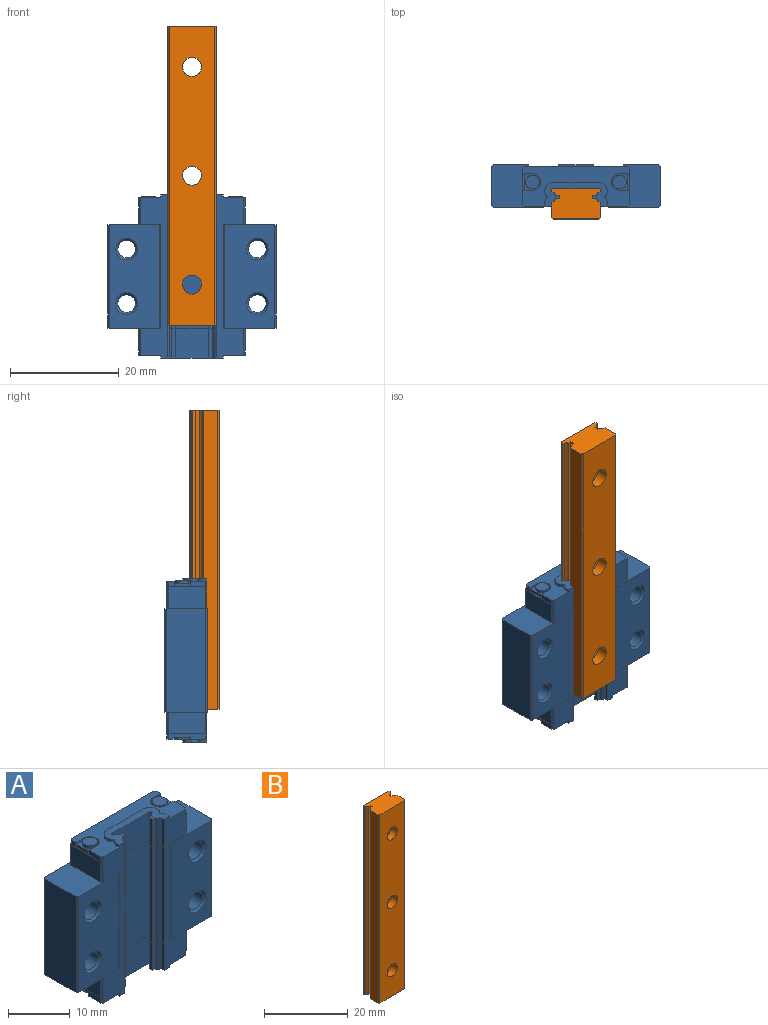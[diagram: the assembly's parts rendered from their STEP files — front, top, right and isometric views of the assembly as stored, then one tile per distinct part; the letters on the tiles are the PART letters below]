
ASSEMBLY  parts=2 mates=1
PART A: 236 faces, bbox 31x7.8x30 mm
  f0: plane 3.05x3mm, normal (0,0,-1), area 3.3mm2, adj f2,f74,f75,f95,f232
  f1: plane 3x0.6mm, normal (1,0,0), area 1.8mm2, adj f62,f68,f69,f235
  f2: plane 3x0.6mm, normal (-1,0,0), area 1.8mm2, adj f0,f62,f74,f75
  f3: plane 5.45x0.66mm, normal (1,0,0), area 3.6mm2, adj f112,f134,f145,f218
  f4: plane 5.45x0.66mm, normal (-1,0,0), area 3.6mm2, adj f19,f112,f144,f218
  f5: plane 19x0.66mm, normal (1,0,0), area 12.5mm2, adj f124,f134,f194,f217
  f6: plane 5.45x0.66mm, normal (1,0,0), area 3.6mm2, adj f113,f134,f157,f195
  f7: plane 5.45x0.66mm, normal (-1,0,0), area 3.6mm2, adj f19,f113,f163,f195
  f8: plane 2.5x2.5mm, normal (0,0,-1), area 4.9mm2, adj f228
  f9: plane 19x9.23mm, normal (0,-1,0), area 150.2mm2, adj f10,f17,f18,f31,f32,f227
  f10: cone r=1.62mm half-angle=45deg, axis (0,-1,0), area 6.1mm2, adj f9,f11
  f11: cylinder r=1.62mm len=7.04mm, axis (0,1,0), area 71.7mm2, adj f10,f12
  f12: cone r=2mm half-angle=45deg, axis (0,1,0), area 6.1mm2, adj f11,f13
  f13: plane 19x6.45mm, normal (0,1,0), area 97.4mm2, adj f12,f14,f15,f31,f32,f225
  f14: plane 19x0.25mm, normal (-0.71,0.71,0), area 6.7mm2, adj f13,f31,f32,f40
  f15: plane 19x0.3mm, normal (0.71,0.71,0), area 8.1mm2, adj f13,f16,f31,f32
  f16: plane 19x7.2mm, normal (1,0,0), area 136.8mm2, adj f15,f17,f31,f32
  f17: plane 19x0.3mm, normal (0.71,-0.71,0), area 8.1mm2, adj f9,f16,f31,f32
  f18: plane 19x0.21mm, normal (-0.42,-0.91,0), area 4.5mm2, adj f9,f19,f31,f32
  f19: plane 30x5mm, normal (0,-1,0), area 75mm2, adj f4,f7,f18,f27,f31,f32,f44,f48
  f20: plane 19x0.21mm, normal (0.42,-0.91,0), area 4.5mm2, adj f21,f31,f32,f134
  f21: plane 19x9.23mm, normal (0,-1,0), area 150.2mm2, adj f20,f22,f31,f32,f221,f224
  f22: plane 19x0.3mm, normal (-0.71,-0.71,0), area 8.1mm2, adj f21,f23,f31,f32
  f23: plane 19x7.2mm, normal (-1,0,0), area 136.8mm2, adj f22,f31,f32,f33
  f24: plane 19x4mm, normal (0,1,0), area 76mm2, adj f25,f30,f31,f96
  f25: plane 4x0.3mm, normal (0.71,0.71,0), area 1.7mm2, adj f24,f26,f31,f96
  f26: plane 6.8x4mm, normal (1,0,0), area 27.2mm2, adj f25,f27,f31,f96
  f27: plane 4x0.3mm, normal (0.71,-0.71,0), area 1.7mm2, adj f19,f26,f31,f96
  f28: plane 4x0.3mm, normal (-0.71,-0.71,0), area 1.7mm2, adj f29,f31,f96,f134
  f29: plane 6.8x4mm, normal (-1,0,0), area 27.2mm2, adj f28,f30,f31,f96
  f30: plane 4x0.3mm, normal (-0.71,0.71,0), area 1.7mm2, adj f24,f29,f31,f96
  f31: plane 31x7.8mm, normal (0,0,1), area 92.9mm2, adj f9,f13,f14,f15,f16,f17,f18,f19
  f32: plane 31x7.8mm, normal (0,0,-1), area 92.9mm2, adj f9,f13,f14,f15,f16,f17,f18,f19
  f33: plane 19x0.3mm, normal (-0.71,0.71,0), area 8.1mm2, adj f23,f31,f32,f34
  f34: plane 19x6.45mm, normal (0,1,0), area 97.4mm2, adj f31,f32,f33,f35,f219,f222
  f35: plane 19x0.25mm, normal (0.71,0.71,0), area 6.7mm2, adj f31,f32,f34,f36
  f36: plane 19x5.1mm, normal (0,1,0), area 96.9mm2, adj f31,f32,f35,f37
  f37: plane 19x0.25mm, normal (-0.71,0.71,0), area 6.7mm2, adj f31,f32,f36,f38
  f38: plane 19x6.3mm, normal (0,1,0), area 119.7mm2, adj f31,f32,f37,f39
  f39: plane 19x0.25mm, normal (0.71,0.71,0), area 6.7mm2, adj f31,f32,f38,f40
  f40: plane 19x5.1mm, normal (0,1,0), area 96.9mm2, adj f14,f31,f32,f39
  f41: plane 4x0.3mm, normal (-0.71,0.71,0), area 1.7mm2, adj f32,f42,f47,f62
  f42: plane 6.8x4mm, normal (-1,0,0), area 27.2mm2, adj f32,f41,f43,f62
  f43: plane 4x0.3mm, normal (-0.71,-0.71,0), area 1.7mm2, adj f32,f42,f62,f134
  f44: plane 4x0.3mm, normal (0.71,-0.71,0), area 1.7mm2, adj f19,f32,f45,f62
  f45: plane 6.8x4mm, normal (1,0,0), area 27.2mm2, adj f32,f44,f46,f62
  f46: plane 4x0.3mm, normal (0.71,0.71,0), area 1.7mm2, adj f32,f45,f47,f62
  f47: plane 19x4mm, normal (0,1,0), area 76mm2, adj f32,f41,f46,f62
  f48: plane 19.5x7.3mm, normal (0,0,1), area 75.5mm2, adj f19,f49,f50,f51,f52,f53,f54,f55
  f49: plane 0.5x0.15mm, normal (-1,0,0), area 0.1mm2, adj f48,f50,f61,f113
  f50: cylinder r=1.5mm len=1.5mm, axis (0,0,-1), area 1.2mm2, adj f48,f49,f51,f113
  f51: plane 8.46x0.5mm, normal (0,1,0), area 4.2mm2, adj f48,f50,f52,f113
  f52: cylinder r=1.5mm len=1.5mm, axis (0,0,-1), area 1.2mm2, adj f48,f51,f53,f113
  f53: plane 0.5x0.15mm, normal (1,0,0), area 0.1mm2, adj f48,f52,f54,f113
  f54: cylinder r=1.3mm len=1.01mm, axis (0,0,-1), area 0.6mm2, adj f48,f53,f55,f113
  f55: cylinder r=0.1mm len=0.5mm, axis (0,0,-1), area 0.1mm2, adj f48,f54,f56,f113
  f56: cylinder r=1.3mm len=1.01mm, axis (0,0,-1), area 0.6mm2, adj f48,f55,f57,f113
  f57: plane 0.62x0.5mm, normal (1,0,0), area 0.3mm2, adj f19,f48,f56,f113
  f58: plane 0.62x0.5mm, normal (-1,0,0), area 0.3mm2, adj f48,f59,f113,f134
  f59: cylinder r=1.3mm len=1.01mm, axis (0,0,-1), area 0.6mm2, adj f48,f58,f60,f113
  f60: cylinder r=0.1mm len=0.5mm, axis (0,0,-1), area 0.1mm2, adj f48,f59,f61,f113
  f61: cylinder r=1.3mm len=1.01mm, axis (0,0,-1), area 0.6mm2, adj f48,f49,f60,f113
  f62: plane 19.6x7.4mm, normal (0,0,-1), area 3.9mm2, adj f1,f2,f19,f41,f42,f43,f44,f45
  f63: plane 1x1mm, normal (-1,0,0), area 1mm2, adj f62,f64,f75,f76
  f64: plane 1x0.3mm, normal (-0.71,0.71,0), area 0.4mm2, adj f62,f63,f65,f76
  f65: plane 18.9x1mm, normal (0,1,0), area 18.9mm2, adj f62,f64,f66,f76
  f66: plane 1x0.3mm, normal (0.71,0.71,0), area 0.4mm2, adj f62,f65,f67,f76
  f67: plane 1x1mm, normal (1,0,0), area 1mm2, adj f62,f66,f68,f76
  f68: plane 1.75x1mm, normal (0,-1,0), area 0.8mm2, adj f1,f62,f67,f76,f94,f235
  f69: plane 1.75x1mm, normal (0,1,0), area 0.8mm2, adj f1,f62,f70,f76,f94,f235
  f70: plane 2.7x1mm, normal (1,0,0), area 2.7mm2, adj f62,f69,f71,f76
  f71: plane 1x0.3mm, normal (0.71,-0.71,0), area 0.4mm2, adj f19,f62,f70,f76
  f72: plane 1x0.3mm, normal (-0.71,-0.71,0), area 0.4mm2, adj f62,f73,f76,f134
  f73: plane 2.7x1mm, normal (-1,0,0), area 2.7mm2, adj f62,f72,f74,f76
  f74: plane 1.75x1mm, normal (0,1,0), area 0.8mm2, adj f0,f2,f62,f73,f76,f95
  f75: plane 1.75x1mm, normal (0,-1,0), area 0.8mm2, adj f0,f2,f62,f63,f76,f95
  f76: plane 19.5x7.3mm, normal (0,0,-1), area 75.5mm2, adj f19,f63,f64,f65,f66,f67,f68,f69
  f77: plane 0.5x0.15mm, normal (-1,0,0), area 0.1mm2, adj f76,f78,f89,f112
  f78: cylinder r=1.5mm len=1.5mm, axis (0,0,1), area 1.2mm2, adj f76,f77,f79,f112
  f79: plane 8.46x0.5mm, normal (0,1,0), area 4.2mm2, adj f76,f78,f80,f112
  f80: cylinder r=1.5mm len=1.5mm, axis (0,0,1), area 1.2mm2, adj f76,f79,f81,f112
  f81: plane 0.5x0.15mm, normal (1,0,0), area 0.1mm2, adj f76,f80,f82,f112
  f82: cylinder r=1.3mm len=1.01mm, axis (0,0,1), area 0.6mm2, adj f76,f81,f83,f112
  f83: cylinder r=0.1mm len=0.5mm, axis (0,0,1), area 0.1mm2, adj f76,f82,f84,f112
  f84: cylinder r=1.3mm len=1.01mm, axis (0,0,1), area 0.6mm2, adj f76,f83,f85,f112
  f85: plane 0.62x0.5mm, normal (1,0,0), area 0.3mm2, adj f19,f76,f84,f112
  f86: plane 0.62x0.5mm, normal (-1,0,0), area 0.3mm2, adj f76,f87,f112,f134
  f87: cylinder r=1.3mm len=1.01mm, axis (0,0,1), area 0.6mm2, adj f76,f86,f88,f112
  f88: cylinder r=0.1mm len=0.5mm, axis (0,0,1), area 0.1mm2, adj f76,f87,f89,f112
  f89: cylinder r=1.3mm len=1.01mm, axis (0,0,1), area 0.6mm2, adj f76,f77,f88,f112
  f90: plane 3x0.6mm, normal (-1,0,0), area 1.8mm2, adj f91,f96,f109,f111
  f91: plane 3.05x3mm, normal (0,0,1), area 3.3mm2, adj f90,f109,f110,f111,f233
  f92: plane 3x0.6mm, normal (1,0,0), area 1.8mm2, adj f93,f96,f102,f104
  f93: plane 3.05x3mm, normal (0,0,1), area 3.3mm2, adj f92,f102,f103,f104,f229
  f94: cylinder r=1.5mm len=3mm, axis (0,0,1), area 1.9mm2, adj f68,f69,f76,f235
  f95: cylinder r=1.5mm len=3mm, axis (0,0,1), area 1.9mm2, adj f0,f74,f75,f76
  f96: plane 19.6x7.4mm, normal (0,0,1), area 3.9mm2, adj f19,f24,f25,f26,f27,f28,f29,f30
  f97: plane 1x1mm, normal (-1,0,0), area 1mm2, adj f48,f96,f98,f111
  f98: plane 1x0.3mm, normal (-0.71,0.71,0), area 0.4mm2, adj f48,f96,f97,f99
  f99: plane 18.9x1mm, normal (0,1,0), area 18.9mm2, adj f48,f96,f98,f100
  f100: plane 1x0.3mm, normal (0.71,0.71,0), area 0.4mm2, adj f48,f96,f99,f101
  f101: plane 1x1mm, normal (1,0,0), area 1mm2, adj f48,f96,f100,f102
  f102: plane 1.75x1mm, normal (0,-1,0), area 0.8mm2, adj f48,f92,f93,f96,f101,f103
  f103: cylinder r=1.5mm len=3mm, axis (0,0,-1), area 1.9mm2, adj f48,f93,f102,f104
  f104: plane 1.75x1mm, normal (0,1,0), area 0.8mm2, adj f48,f92,f93,f96,f103,f105
  f105: plane 2.7x1mm, normal (1,0,0), area 2.7mm2, adj f48,f96,f104,f106
  f106: plane 1x0.3mm, normal (0.71,-0.71,0), area 0.4mm2, adj f19,f48,f96,f105
  f107: plane 1x0.3mm, normal (-0.71,-0.71,0), area 0.4mm2, adj f48,f96,f108,f134
  f108: plane 2.7x1mm, normal (-1,0,0), area 2.7mm2, adj f48,f96,f107,f109
  f109: plane 1.75x1mm, normal (0,1,0), area 0.8mm2, adj f48,f90,f91,f96,f108,f110
  f110: cylinder r=1.5mm len=3mm, axis (0,0,-1), area 1.9mm2, adj f48,f91,f109,f111
  f111: plane 1.75x1mm, normal (0,-1,0), area 0.8mm2, adj f48,f90,f91,f96,f97,f110
  f112: plane 11.46x4.43mm, normal (0,0,-1), area 23.6mm2, adj f3,f4,f19,f77,f78,f79,f80,f81
  f113: plane 11.46x4.43mm, normal (0,0,1), area 23.6mm2, adj f6,f7,f19,f49,f50,f51,f52,f53
  f114: plane 19x8.6mm, normal (0,-1,0), area 163.4mm2, adj f115,f132,f194,f217
  f115: plane 19x0.2mm, normal (-0.71,-0.71,0), area 5.4mm2, adj f114,f116,f194,f217
  f116: plane 19x0.26mm, normal (-1,0,0), area 4.9mm2, adj f115,f117,f194,f217
  f117: plane 19x0.28mm, normal (-0.5,0.87,0), area 6.1mm2, adj f116,f118,f194,f217
  f118: cylinder r=1.1mm len=19mm, axis (0,0,1), area 13.7mm2, adj f117,f119,f194,f217
  f119: plane 19x0.66mm, normal (0,1,0), area 12.4mm2, adj f118,f120,f194,f217
  f120: plane 19x0.7mm, normal (-1,0,0), area 13.3mm2, adj f119,f121,f194,f217
  f121: plane 19x0.66mm, normal (0,-1,0), area 12.4mm2, adj f120,f122,f194,f217
  f122: cylinder r=1.1mm len=19mm, axis (0,0,1), area 13.7mm2, adj f121,f123,f194,f217
  f123: plane 19x0.28mm, normal (-0.5,-0.87,0), area 6.1mm2, adj f122,f133,f194,f217
  f124: plane 19x0.28mm, normal (0.5,-0.87,0), area 6.1mm2, adj f5,f125,f194,f217
  f125: cylinder r=1.1mm len=19mm, axis (0,0,1), area 13.7mm2, adj f124,f126,f194,f217
  f126: plane 19x0.66mm, normal (0,-1,0), area 12.4mm2, adj f125,f127,f194,f217
  f127: plane 19x0.7mm, normal (1,0,0), area 13.3mm2, adj f126,f128,f194,f217
  f128: plane 19x0.66mm, normal (0,1,0), area 12.4mm2, adj f127,f129,f194,f217
  f129: cylinder r=1.1mm len=19mm, axis (0,0,1), area 13.7mm2, adj f128,f130,f194,f217
  f130: plane 19x0.28mm, normal (0.5,0.87,0), area 6.1mm2, adj f129,f131,f194,f217
  f131: plane 19x0.26mm, normal (1,0,0), area 4.9mm2, adj f130,f132,f194,f217
  f132: plane 19x0.2mm, normal (0.71,-0.71,0), area 5.4mm2, adj f114,f131,f194,f217
  f133: plane 19x0.66mm, normal (-1,0,0), area 12.5mm2, adj f19,f123,f194,f217
  f134: plane 30x5mm, normal (0,-1,0), area 75mm2, adj f3,f5,f6,f20,f28,f31,f32,f43
  f135: plane 8.6x5.45mm, normal (0,-1,0), area 46.9mm2, adj f112,f136,f153,f218
  f136: plane 5.45x0.2mm, normal (-0.71,-0.71,0), area 1.5mm2, adj f112,f135,f137,f218
  f137: plane 5.45x0.26mm, normal (-1,0,0), area 1.4mm2, adj f112,f136,f138,f218
  f138: plane 5.45x0.28mm, normal (-0.5,0.87,0), area 1.8mm2, adj f112,f137,f139,f218
  f139: cylinder r=1.1mm len=5.45mm, axis (0,0,1), area 3.9mm2, adj f112,f138,f140,f218
  f140: plane 5.45x0.66mm, normal (0,1,0), area 3.6mm2, adj f112,f139,f141,f218
  f141: plane 5.45x0.7mm, normal (-1,0,0), area 3.8mm2, adj f112,f140,f142,f218
  f142: plane 5.45x0.66mm, normal (0,-1,0), area 3.6mm2, adj f112,f141,f143,f218
  f143: cylinder r=1.1mm len=5.45mm, axis (0,0,1), area 3.9mm2, adj f112,f142,f144,f218
  f144: plane 5.45x0.28mm, normal (-0.5,-0.87,0), area 1.8mm2, adj f4,f112,f143,f218
  f145: plane 5.45x0.28mm, normal (0.5,-0.87,0), area 1.8mm2, adj f3,f112,f146,f218
  f146: cylinder r=1.1mm len=5.45mm, axis (0,0,1), area 3.9mm2, adj f112,f145,f147,f218
  f147: plane 5.45x0.66mm, normal (0,-1,0), area 3.6mm2, adj f112,f146,f148,f218
  f148: plane 5.45x0.7mm, normal (1,0,0), area 3.8mm2, adj f112,f147,f149,f218
  f149: plane 5.45x0.66mm, normal (0,1,0), area 3.6mm2, adj f112,f148,f150,f218
  f150: cylinder r=1.1mm len=5.45mm, axis (0,0,1), area 3.9mm2, adj f112,f149,f151,f218
  f151: plane 5.45x0.28mm, normal (0.5,0.87,0), area 1.8mm2, adj f112,f150,f152,f218
  f152: plane 5.45x0.26mm, normal (1,0,0), area 1.4mm2, adj f112,f151,f153,f218
  f153: plane 5.45x0.2mm, normal (0.71,-0.71,0), area 1.5mm2, adj f112,f135,f152,f218
  f154: plane 5.45x0.2mm, normal (0.71,-0.71,0), area 1.5mm2, adj f113,f155,f172,f195
  f155: plane 5.45x0.26mm, normal (1,0,0), area 1.4mm2, adj f113,f154,f162,f195
  f156: cylinder r=1.1mm len=5.45mm, axis (0,0,1), area 3.9mm2, adj f113,f157,f158,f195
  f157: plane 5.45x0.28mm, normal (0.5,-0.87,0), area 1.8mm2, adj f6,f113,f156,f195
  f158: plane 5.45x0.66mm, normal (0,-1,0), area 3.6mm2, adj f113,f156,f159,f195
  f159: plane 5.45x0.7mm, normal (1,0,0), area 3.8mm2, adj f113,f158,f160,f195
  f160: plane 5.45x0.66mm, normal (0,1,0), area 3.6mm2, adj f113,f159,f161,f195
  f161: cylinder r=1.1mm len=5.45mm, axis (0,0,1), area 3.9mm2, adj f113,f160,f162,f195
  f162: plane 5.45x0.28mm, normal (0.5,0.87,0), area 1.8mm2, adj f113,f155,f161,f195
  f163: plane 5.45x0.28mm, normal (-0.5,-0.87,0), area 1.8mm2, adj f7,f113,f164,f195
  f164: cylinder r=1.1mm len=5.45mm, axis (0,0,1), area 3.9mm2, adj f113,f163,f165,f195
  f165: plane 5.45x0.66mm, normal (0,-1,0), area 3.6mm2, adj f113,f164,f166,f195
  f166: plane 5.45x0.7mm, normal (-1,0,0), area 3.8mm2, adj f113,f165,f167,f195
  f167: plane 5.45x0.66mm, normal (0,1,0), area 3.6mm2, adj f113,f166,f168,f195
  f168: cylinder r=1.1mm len=5.45mm, axis (0,0,1), area 3.9mm2, adj f113,f167,f169,f195
  f169: plane 5.45x0.28mm, normal (-0.5,0.87,0), area 1.8mm2, adj f113,f168,f170,f195
  f170: plane 5.45x0.26mm, normal (-1,0,0), area 1.4mm2, adj f113,f169,f171,f195
  f171: plane 5.45x0.2mm, normal (-0.71,-0.71,0), area 1.5mm2, adj f113,f170,f172,f195
  f172: plane 8.6x5.45mm, normal (0,-1,0), area 46.9mm2, adj f113,f154,f171,f195
  f173: plane 0.71x0.05mm, normal (1,0,0), area 0mm2, adj f134,f174,f194,f195
  f174: plane 0.25x0.12mm, normal (0.45,-0.89,0), area 0mm2, adj f173,f175,f194,f195
  f175: cylinder r=1.05mm len=0.57mm, axis (0,0,1), area 0mm2, adj f174,f176,f194,f195
  f176: plane 0.64x0.05mm, normal (0,-1,0), area 0mm2, adj f175,f177,f194,f195
  f177: plane 0.6x0.05mm, normal (1,0,0), area 0mm2, adj f176,f178,f194,f195
  f178: plane 0.64x0.05mm, normal (0,1,0), area 0mm2, adj f177,f179,f194,f195
  f179: cylinder r=1.05mm len=0.57mm, axis (0,0,1), area 0mm2, adj f178,f180,f194,f195
  f180: plane 0.25x0.12mm, normal (0.45,0.89,0), area 0mm2, adj f179,f181,f194,f195
  f181: plane 0.36x0.05mm, normal (1,0,0), area 0mm2, adj f180,f182,f194,f195
  f182: plane 0.2x0.2mm, normal (0.71,-0.71,0), area 0mm2, adj f181,f183,f194,f195
  f183: plane 8.7x0.05mm, normal (0,-1,0), area 0.4mm2, adj f182,f184,f194,f195
  f184: plane 0.2x0.2mm, normal (-0.71,-0.71,0), area 0mm2, adj f183,f185,f194,f195
  f185: plane 0.36x0.05mm, normal (-1,0,0), area 0mm2, adj f184,f186,f194,f195
  f186: plane 0.25x0.12mm, normal (-0.45,0.89,0), area 0mm2, adj f185,f187,f194,f195
  f187: cylinder r=1.05mm len=0.57mm, axis (0,0,1), area 0mm2, adj f186,f188,f194,f195
  f188: plane 0.64x0.05mm, normal (0,1,0), area 0mm2, adj f187,f189,f194,f195
  f189: plane 0.6x0.05mm, normal (-1,0,0), area 0mm2, adj f188,f190,f194,f195
  f190: plane 0.64x0.05mm, normal (0,-1,0), area 0mm2, adj f189,f191,f194,f195
  f191: cylinder r=1.05mm len=0.57mm, axis (0,0,1), area 0mm2, adj f190,f192,f194,f195
  f192: plane 0.25x0.12mm, normal (-0.45,-0.89,0), area 0mm2, adj f191,f193,f194,f195
  f193: plane 0.71x0.05mm, normal (-1,0,0), area 0mm2, adj f19,f192,f194,f195
  f194: plane 9.1x3.25mm, normal (0,0,1), area 1mm2, adj f5,f19,f114,f115,f116,f117,f118,f119
  f195: plane 9.1x3.25mm, normal (0,0,-1), area 1mm2, adj f6,f7,f19,f134,f154,f155,f156,f157
  f196: plane 0.71x0.05mm, normal (1,0,0), area 0mm2, adj f134,f197,f217,f218
  f197: plane 0.25x0.12mm, normal (0.45,-0.89,0), area 0mm2, adj f196,f198,f217,f218
  f198: cylinder r=1.05mm len=0.57mm, axis (0,0,-1), area 0mm2, adj f197,f199,f217,f218
  f199: plane 0.64x0.05mm, normal (0,-1,0), area 0mm2, adj f198,f200,f217,f218
  f200: plane 0.6x0.05mm, normal (1,0,0), area 0mm2, adj f199,f201,f217,f218
  f201: plane 0.64x0.05mm, normal (0,1,0), area 0mm2, adj f200,f202,f217,f218
  f202: cylinder r=1.05mm len=0.57mm, axis (0,0,-1), area 0mm2, adj f201,f203,f217,f218
  f203: plane 0.25x0.12mm, normal (0.45,0.89,0), area 0mm2, adj f202,f204,f217,f218
  f204: plane 0.36x0.05mm, normal (1,0,0), area 0mm2, adj f203,f205,f217,f218
  f205: plane 0.2x0.2mm, normal (0.71,-0.71,0), area 0mm2, adj f204,f206,f217,f218
  f206: plane 8.7x0.05mm, normal (0,-1,0), area 0.4mm2, adj f205,f207,f217,f218
  f207: plane 0.2x0.2mm, normal (-0.71,-0.71,0), area 0mm2, adj f206,f208,f217,f218
  f208: plane 0.36x0.05mm, normal (-1,0,0), area 0mm2, adj f207,f209,f217,f218
  f209: plane 0.25x0.12mm, normal (-0.45,0.89,0), area 0mm2, adj f208,f210,f217,f218
  f210: cylinder r=1.05mm len=0.57mm, axis (0,0,-1), area 0mm2, adj f209,f211,f217,f218
  f211: plane 0.64x0.05mm, normal (0,1,0), area 0mm2, adj f210,f212,f217,f218
  f212: plane 0.6x0.05mm, normal (-1,0,0), area 0mm2, adj f211,f213,f217,f218
  f213: plane 0.64x0.05mm, normal (0,-1,0), area 0mm2, adj f212,f214,f217,f218
  f214: cylinder r=1.05mm len=0.57mm, axis (0,0,-1), area 0mm2, adj f213,f215,f217,f218
  f215: plane 0.25x0.12mm, normal (-0.45,-0.89,0), area 0mm2, adj f214,f216,f217,f218
  f216: plane 0.71x0.05mm, normal (-1,0,0), area 0mm2, adj f19,f215,f217,f218
  f217: plane 9.1x3.25mm, normal (0,0,-1), area 1mm2, adj f5,f19,f114,f115,f116,f117,f118,f119
  f218: plane 9.1x3.25mm, normal (0,0,1), area 1mm2, adj f3,f4,f19,f134,f135,f136,f137,f138
  f219: cone r=2mm half-angle=45deg, axis (0,1,0), area 6.1mm2, adj f34,f220
  f220: cylinder r=1.62mm len=7.04mm, axis (0,1,0), area 71.7mm2, adj f219,f221
  f221: cone r=1.62mm half-angle=45deg, axis (0,-1,0), area 6.1mm2, adj f21,f220
  f222: cone r=2mm half-angle=45deg, axis (0,1,0), area 6.1mm2, adj f34,f223
  f223: cylinder r=1.62mm len=7.04mm, axis (0,1,0), area 71.7mm2, adj f222,f224
  f224: cone r=1.62mm half-angle=45deg, axis (0,-1,0), area 6.1mm2, adj f21,f223
  f225: cone r=2mm half-angle=45deg, axis (0,1,0), area 6.1mm2, adj f13,f226
  f226: cylinder r=1.62mm len=7.04mm, axis (0,1,0), area 71.7mm2, adj f225,f227
  f227: cone r=1.62mm half-angle=45deg, axis (0,-1,0), area 6.1mm2, adj f9,f226
  f228: cylinder r=1.25mm len=2.5mm, axis (0,0,1), area 3.9mm2, adj f8,f235
  f229: cylinder r=1.25mm len=2.5mm, axis (0,0,1), area 3.9mm2, adj f93,f230
  f230: plane 2.5x2.5mm, normal (0,0,1), area 4.9mm2, adj f229
  f231: plane 2.5x2.5mm, normal (0,0,-1), area 4.9mm2, adj f232
  f232: cylinder r=1.25mm len=2.5mm, axis (0,0,1), area 3.9mm2, adj f0,f231
  f233: cylinder r=1.25mm len=2.5mm, axis (0,0,1), area 3.9mm2, adj f91,f234
  f234: plane 2.5x2.5mm, normal (0,0,1), area 4.9mm2, adj f233
  f235: plane 3.05x3mm, normal (0,0,-1), area 3.3mm2, adj f1,f68,f69,f94,f228
PART B: 35 faces, bbox 9x5.5x55 mm
  f0: plane 55x0.28mm, normal (0.5,-0.87,0), area 17.7mm2, adj f1,f2,f6,f8
  f1: plane 55x0.26mm, normal (1,0,0), area 14.1mm2, adj f0,f6,f7,f8
  f2: cylinder r=1.1mm len=55mm, axis (0,0,1), area 39.7mm2, adj f0,f6,f8,f34
  f3: plane 55x0.2mm, normal (-0.71,0.71,0), area 15.6mm2, adj f4,f5,f6,f8
  f4: plane 55x0.26mm, normal (-1,0,0), area 14.1mm2, adj f3,f6,f8,f22
  f5: plane 55x8.6mm, normal (0,1,0), area 388.2mm2, adj f3,f6,f7,f8,f9,f12,f15
  f6: plane 9x5.5mm, normal (0,0,1), area 46.1mm2, adj f0,f1,f2,f3,f4,f5,f7,f18
  f7: plane 55x0.2mm, normal (0.71,0.71,0), area 15.6mm2, adj f1,f5,f6,f8
  f8: plane 9x5.5mm, normal (0,0,-1), area 46.1mm2, adj f0,f1,f2,f3,f4,f5,f7,f18
  f9: cylinder r=3mm len=6mm, axis (0,1,0), area 66mm2, adj f5,f10
  f10: plane 6x6mm, normal (0,1,0), area 18.7mm2, adj f9,f11
  f11: cylinder r=1.75mm len=3.5mm, axis (0,1,0), area 22mm2, adj f10,f18
  f12: cylinder r=3mm len=6mm, axis (0,1,0), area 66mm2, adj f5,f13
  f13: plane 6x6mm, normal (0,1,0), area 18.7mm2, adj f12,f14
  f14: cylinder r=1.75mm len=3.5mm, axis (0,1,0), area 22mm2, adj f13,f18
  f15: cylinder r=3mm len=6mm, axis (0,1,0), area 66mm2, adj f5,f16
  f16: plane 6x6mm, normal (0,1,0), area 18.7mm2, adj f15,f17
  f17: cylinder r=1.75mm len=3.5mm, axis (0,1,0), area 22mm2, adj f16,f18
  f18: plane 55x8.4mm, normal (0,-1,0), area 433.1mm2, adj f6,f8,f11,f14,f17,f27,f28
  f19: plane 55x0.66mm, normal (0,-1,0), area 36mm2, adj f6,f8,f20,f21
  f20: plane 55x0.7mm, normal (-1,0,0), area 38.5mm2, adj f6,f8,f19,f23
  f21: cylinder r=1.1mm len=55mm, axis (0,0,1), area 39.7mm2, adj f6,f8,f19,f22
  f22: plane 55x0.28mm, normal (-0.5,-0.87,0), area 17.7mm2, adj f4,f6,f8,f21
  f23: plane 55x0.66mm, normal (0,1,0), area 36mm2, adj f6,f8,f20,f24
  f24: cylinder r=1.1mm len=55mm, axis (0,0,1), area 39.7mm2, adj f6,f8,f23,f25
  f25: plane 55x0.28mm, normal (-0.5,0.87,0), area 17.7mm2, adj f6,f8,f24,f26
  f26: plane 55x2.66mm, normal (-1,0,0), area 146.1mm2, adj f6,f8,f25,f27
  f27: plane 55x0.3mm, normal (-0.71,-0.71,0), area 23.3mm2, adj f6,f8,f18,f26
  f28: plane 55x0.3mm, normal (0.71,-0.71,0), area 23.3mm2, adj f6,f8,f18,f29
  f29: plane 55x2.66mm, normal (1,0,0), area 146.1mm2, adj f6,f8,f28,f30
  f30: plane 55x0.28mm, normal (0.5,0.87,0), area 17.7mm2, adj f6,f8,f29,f31
  f31: cylinder r=1.1mm len=55mm, axis (0,0,1), area 39.7mm2, adj f6,f8,f30,f32
  f32: plane 55x0.66mm, normal (0,1,0), area 36mm2, adj f6,f8,f31,f33
  f33: plane 55x0.7mm, normal (1,0,0), area 38.5mm2, adj f6,f8,f32,f34
  f34: plane 55x0.66mm, normal (0,-1,0), area 36mm2, adj f2,f6,f8,f33
PLACE A rot(axis=(0,1,0),180deg) t=(0,0,-18.48)mm
PLACE B at identity fixed
MATE slider A.f112 <-> B.f6  axis (0,0,1) through (0,5.5,-3.48)mm
